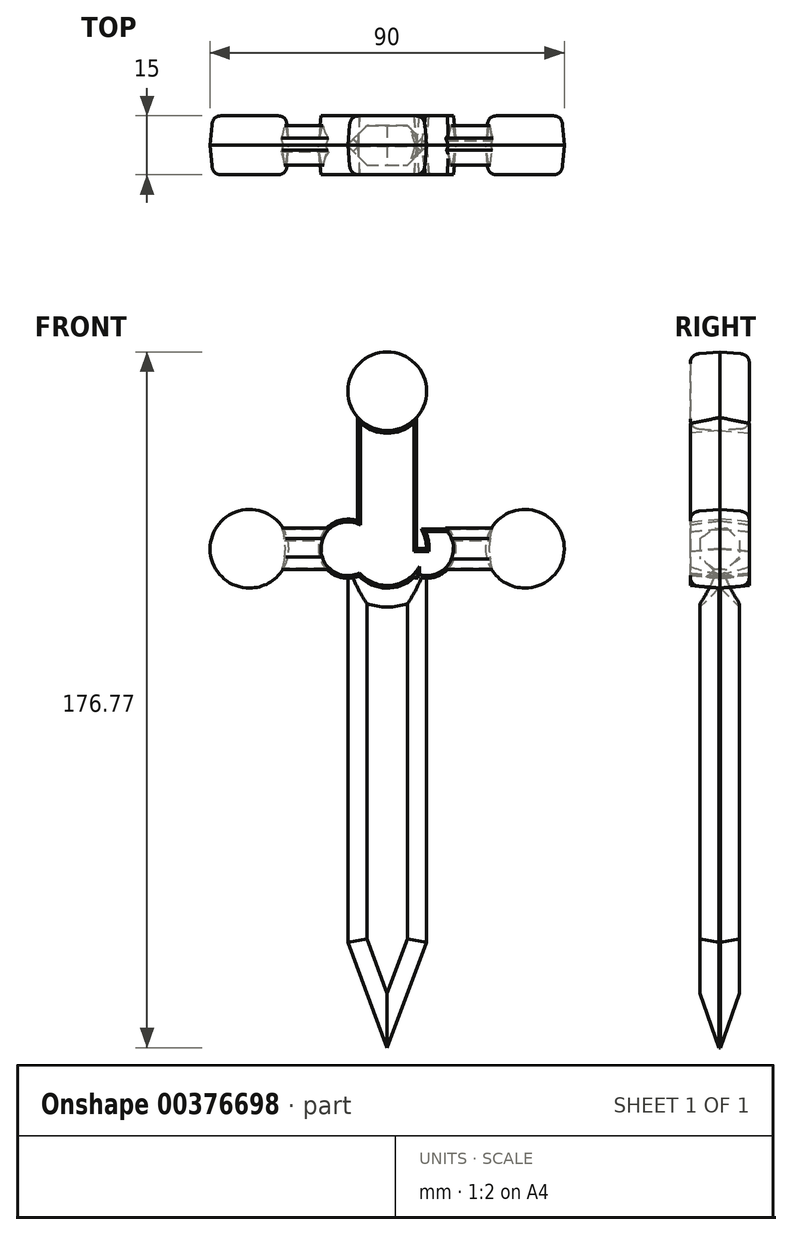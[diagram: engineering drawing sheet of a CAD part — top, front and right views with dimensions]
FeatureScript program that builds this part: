
annotation { "Feature Type Name" : "Feature", "Feature Type Description" : "" }
export const myFeature = defineFeature(function(context is Context, id is Id, definition is map)
    precondition{}
    {
        {
            var Q0;
            Q0=qCreatedBy(makeId("Front.planeOp"),FACE);
            var sketch = newSketch(context, id + "F0", { "sketchPlane" : qUnion([Q0])});
            skLineSegment(sketch, "E0.bottom", {"start": v(10, 50) * mm, "end": v(-10, 50) * mm});
            skLineSegment(sketch, "E0.top", {"start": v(10, -50) * mm, "end": v(-10, -50) * mm});
            skLineSegment(sketch, "E0.left", {"start": v(10, 50) * mm, "end": v(10, -50) * mm});
            skLineSegment(sketch, "E0.right", {"start": v(-10, 50) * mm, "end": v(-10, -50) * mm});
            skPoint(sketch, "E0.middle", {"position": v(0, 0) * mm});
            skCircle(sketch, "E1", {"center": v(0, 50) * mm, "radius": 10 * mm});
            skLineSegment(sketch, "E2.bottom", {"start": v(35, 55) * mm, "end": v(-35, 55) * mm});
            skLineSegment(sketch, "E2.top", {"start": v(35, 45) * mm, "end": v(-35, 45) * mm});
            skLineSegment(sketch, "E2.left", {"start": v(35, 55) * mm, "end": v(35, 45) * mm});
            skLineSegment(sketch, "E2.right", {"start": v(-35, 55) * mm, "end": v(-35, 45) * mm});
            skCircle(sketch, "E3", {"center": v(-35, 50) * mm, "radius": 10 * mm});
            skCircle(sketch, "E4", {"center": v(-10, 50) * mm, "radius": 7.5 * mm});
            skCircle(sketch, "E5", {"center": v(35, 50) * mm, "radius": 10 * mm});
            skCircle(sketch, "E6", {"center": v(10, 50) * mm, "radius": 7.5 * mm});
            skLineSegment(sketch, "E7.bottom", {"start": v(7.5, 90) * mm, "end": v(-7.5, 90) * mm});
            skLineSegment(sketch, "E7.top", {"start": v(7.5, 30) * mm, "end": v(-7.5, 30) * mm});
            skLineSegment(sketch, "E7.left", {"start": v(7.5, 90) * mm, "end": v(7.5, 30) * mm});
            skLineSegment(sketch, "E7.right", {"start": v(-7.5, 90) * mm, "end": v(-7.5, 30) * mm});
            skPoint(sketch, "E7.middle", {"position": v(0, 60) * mm});
            skCircle(sketch, "E8", {"center": v(0, 90) * mm, "radius": 10 * mm});
            skLineSegment(sketch, "E9", {"start": v(-10, -50) * mm, "end": v(0, -76.77) * mm});
            skLineSegment(sketch, "E10", {"start": v(0, -76.77) * mm, "end": v(10, -50) * mm});
            skSolve(sketch);
        }
        {
            var Q0;
            {var subQ0=sQuery(id+"F0.wireOp",EDGE,"E1");var subQ5=sQuery(id+"F0.wireOp",EDGE,"E2.bottom");var subQ6=makeQuery(id+"F0.imprint","INTERSECT",VERTEX,{"disambiguationData":[OD(1.0)],"derivedFrom":[subQ0,subQ5]});Q0=makeQuery(id+"F0.imprint","IMPRINT",FACE,{"disambiguationData":[TD([[makeQuery(id+"F0.imprint","IMPRINT",EDGE,{"disambiguationData":[TD([[subQ6,1.0]])],"derivedFrom":subQ5}),1.0]])]});}
            var Q1;
            {var subQ0=sQuery(id+"F0.wireOp",EDGE,"E1");var subQ5=sQuery(id+"F0.wireOp",EDGE,"E2.top");var subQ6=makeQuery(id+"F0.imprint","INTERSECT",VERTEX,{"disambiguationData":[OD(0.0)],"derivedFrom":[subQ0,subQ5]});Q1=makeQuery(id+"F0.imprint","IMPRINT",FACE,{"disambiguationData":[TD([[makeQuery(id+"F0.imprint","IMPRINT",EDGE,{"disambiguationData":[TD([[subQ6,1.0]])],"derivedFrom":subQ5}),-1.0]])]});}
            var Q2;
            {var subQ1=sQuery(id+"F0.wireOp",EDGE,"E0.right");var subQ3=sQuery(id+"F0.wireOp",EDGE,"E2.top");var subQ4=makeQuery(id+"F0.imprint","INTERSECT",VERTEX,{"derivedFrom":[subQ1,subQ3]});Q2=makeQuery(id+"F0.imprint","IMPRINT",FACE,{"disambiguationData":[TD([[makeQuery(id+"F0.imprint","IMPRINT",EDGE,{"disambiguationData":[TD([[subQ4,1.0]])],"derivedFrom":subQ3}),-1.0]])]});}
            var Q3;
            {var subQ0=sQuery(id+"F0.wireOp",EDGE,"E7.right");var subQ1=sQuery(id+"F0.wireOp",EDGE,"E1");var subQ2=makeQuery(id+"F0.imprint","INTERSECT",VERTEX,{"disambiguationData":[OD(1.0)],"derivedFrom":[subQ1,subQ0]});Q3=makeQuery(id+"F0.imprint","IMPRINT",FACE,{"disambiguationData":[TD([[makeQuery(id+"F0.imprint","IMPRINT",EDGE,{"disambiguationData":[TD([[subQ2,-1.0]])],"derivedFrom":subQ1}),1.0]])]});}
            var Q4;
            {var subQ1=sQuery(id+"F0.wireOp",EDGE,"E0.right");var subQ5=sQuery(id+"F0.wireOp",EDGE,"E4");var subQ6=makeQuery(id+"F0.imprint","INTERSECT",VERTEX,{"derivedFrom":[subQ1,subQ5]});Q4=makeQuery(id+"F0.imprint","IMPRINT",FACE,{"disambiguationData":[TD([[makeQuery(id+"F0.imprint","IMPRINT",EDGE,{"disambiguationData":[TD([[subQ6,1.0]])],"derivedFrom":subQ1}),1.0]])]});}
            var Q5;
            {var subQ0=sQuery(id+"F0.wireOp",EDGE,"E4");var subQ1=sQuery(id+"F0.wireOp",EDGE,"E0.right");var subQ2=makeQuery(id+"F0.imprint","INTERSECT",VERTEX,{"derivedFrom":[subQ1,subQ0]});Q5=makeQuery(id+"F0.imprint","IMPRINT",FACE,{"disambiguationData":[TD([[makeQuery(id+"F0.imprint","IMPRINT",EDGE,{"disambiguationData":[TD([[subQ2,1.0]])],"derivedFrom":subQ1}),-1.0]])]});}
            var Q6;
            {var subQ0=sQuery(id+"F0.wireOp",EDGE,"E2.top");var subQ1=sQuery(id+"F0.wireOp",EDGE,"E1");var subQ2=makeQuery(id+"F0.imprint","INTERSECT",VERTEX,{"disambiguationData":[OD(0.0)],"derivedFrom":[subQ1,subQ0]});Q6=makeQuery(id+"F0.imprint","IMPRINT",FACE,{"disambiguationData":[TD([[makeQuery(id+"F0.imprint","IMPRINT",EDGE,{"disambiguationData":[TD([[subQ2,-1.0]])],"derivedFrom":subQ1}),1.0]])]});}
            var Q7;
            {var subQ0=sQuery(id+"F0.wireOp",EDGE,"E4");var subQ1=sQuery(id+"F0.wireOp",EDGE,"E0.bottom");var subQ2=makeQuery(id+"F0.imprint","INTERSECT",VERTEX,{"derivedFrom":[subQ1,subQ0]});Q7=makeQuery(id+"F0.imprint","IMPRINT",FACE,{"disambiguationData":[TD([[makeQuery(id+"F0.imprint","IMPRINT",EDGE,{"disambiguationData":[TD([[subQ2,-1.0]])],"derivedFrom":subQ1}),1.0]])]});}
            var Q8;
            {var subQ0=sQuery(id+"F0.wireOp",EDGE,"E4");var subQ5=sQuery(id+"F0.wireOp",EDGE,"E2.bottom");var subQ6=makeQuery(id+"F0.imprint","INTERSECT",VERTEX,{"disambiguationData":[OD(0.0)],"derivedFrom":[subQ5,subQ0]});Q8=makeQuery(id+"F0.imprint","IMPRINT",FACE,{"disambiguationData":[TD([[makeQuery(id+"F0.imprint","IMPRINT",EDGE,{"disambiguationData":[TD([[subQ6,1.0]])],"derivedFrom":subQ5}),1.0]])]});}
            var Q9;
            {var subQ0=sQuery(id+"F0.wireOp",EDGE,"E6");var subQ1=sQuery(id+"F0.wireOp",EDGE,"E0.left");var subQ2=makeQuery(id+"F0.imprint","INTERSECT",VERTEX,{"derivedFrom":[subQ1,subQ0]});Q9=makeQuery(id+"F0.imprint","IMPRINT",FACE,{"disambiguationData":[TD([[makeQuery(id+"F0.imprint","IMPRINT",EDGE,{"disambiguationData":[TD([[subQ2,1.0]])],"derivedFrom":subQ1}),1.0]])]});}
            var Q10;
            {var subQ0=sQuery(id+"F0.wireOp",EDGE,"E6");var subQ1=sQuery(id+"F0.wireOp",EDGE,"E1");var subQ2=makeQuery(id+"F0.imprint","INTERSECT",VERTEX,{"disambiguationData":[OD(0.0)],"derivedFrom":[subQ1,subQ0]});Q10=makeQuery(id+"F0.imprint","IMPRINT",FACE,{"disambiguationData":[TD([[makeQuery(id+"F0.imprint","IMPRINT",EDGE,{"disambiguationData":[TD([[subQ2,-1.0]])],"derivedFrom":subQ1}),1.0]])]});}
            var Q11;
            {var subQ0=sQuery(id+"F0.wireOp",EDGE,"E2.left");Q11=makeQuery(id+"F0.imprint","IMPRINT",FACE,{"disambiguationData":[TD([[makeQuery(id+"F0.imprint","IMPRINT",EDGE,{"derivedFrom":subQ0}),-1.0]])]});}
            var Q12;
            {var subQ0=sQuery(id+"F0.wireOp",EDGE,"E2.right");Q12=makeQuery(id+"F0.imprint","IMPRINT",FACE,{"disambiguationData":[TD([[makeQuery(id+"F0.imprint","IMPRINT",EDGE,{"derivedFrom":subQ0}),1.0]])]});}
            var Q13;
            {var subQ0=sQuery(id+"F0.wireOp",EDGE,"E2.right");Q13=makeQuery(id+"F0.imprint","IMPRINT",FACE,{"disambiguationData":[TD([[makeQuery(id+"F0.imprint","IMPRINT",EDGE,{"derivedFrom":subQ0}),-1.0]])]});}
            var Q14;
            {var subQ0=sQuery(id+"F0.wireOp",EDGE,"E2.left");Q14=makeQuery(id+"F0.imprint","IMPRINT",FACE,{"disambiguationData":[TD([[makeQuery(id+"F0.imprint","IMPRINT",EDGE,{"derivedFrom":subQ0}),1.0]])]});}
            var Q15;
            {var subQ0=sQuery(id+"F0.wireOp",EDGE,"E2.bottom");var subQ1=sQuery(id+"F0.wireOp",EDGE,"E1");var subQ2=makeQuery(id+"F0.imprint","INTERSECT",VERTEX,{"disambiguationData":[OD(0.0)],"derivedFrom":[subQ1,subQ0]});Q15=makeQuery(id+"F0.imprint","IMPRINT",FACE,{"disambiguationData":[TD([[makeQuery(id+"F0.imprint","IMPRINT",EDGE,{"disambiguationData":[TD([[subQ2,-1.0]])],"derivedFrom":subQ1}),-1.0]])]});}
            var Q16;
            {var subQ0=sQuery(id+"F0.wireOp",EDGE,"E6");var subQ1=sQuery(id+"F0.wireOp",EDGE,"E0.bottom");var subQ2=makeQuery(id+"F0.imprint","INTERSECT",VERTEX,{"derivedFrom":[subQ1,subQ0]});Q16=makeQuery(id+"F0.imprint","IMPRINT",FACE,{"disambiguationData":[TD([[makeQuery(id+"F0.imprint","IMPRINT",EDGE,{"disambiguationData":[TD([[subQ2,-1.0]])],"derivedFrom":subQ1}),-1.0]])]});}
            var Q17;
            {var subQ0=sQuery(id+"F0.wireOp",EDGE,"E6");var subQ1=sQuery(id+"F0.wireOp",EDGE,"E0.left");var subQ2=makeQuery(id+"F0.imprint","INTERSECT",VERTEX,{"derivedFrom":[subQ1,subQ0]});Q17=makeQuery(id+"F0.imprint","IMPRINT",FACE,{"disambiguationData":[TD([[makeQuery(id+"F0.imprint","IMPRINT",EDGE,{"disambiguationData":[TD([[subQ2,1.0]])],"derivedFrom":subQ1}),-1.0]])]});}
            var Q18;
            {var subQ0=sQuery(id+"F0.wireOp",EDGE,"E4");var subQ1=sQuery(id+"F0.wireOp",EDGE,"E1");var subQ2=makeQuery(id+"F0.imprint","INTERSECT",VERTEX,{"disambiguationData":[OD(1.0)],"derivedFrom":[subQ1,subQ0]});Q18=makeQuery(id+"F0.imprint","IMPRINT",FACE,{"disambiguationData":[TD([[makeQuery(id+"F0.imprint","IMPRINT",EDGE,{"disambiguationData":[TD([[subQ2,-1.0]])],"derivedFrom":subQ1}),1.0]])]});}
            var Q19;
            {var subQ0=sQuery(id+"F0.wireOp",EDGE,"E1");var subQ5=sQuery(id+"F0.wireOp",EDGE,"E2.bottom");var subQ6=makeQuery(id+"F0.imprint","INTERSECT",VERTEX,{"disambiguationData":[OD(0.0)],"derivedFrom":[subQ0,subQ5]});Q19=makeQuery(id+"F0.imprint","IMPRINT",FACE,{"disambiguationData":[TD([[makeQuery(id+"F0.imprint","IMPRINT",EDGE,{"disambiguationData":[TD([[subQ6,-1.0]])],"derivedFrom":subQ5}),1.0]])]});}
            var Q20;
            {var subQ0=sQuery(id+"F0.wireOp",EDGE,"E6");var subQ1=sQuery(id+"F0.wireOp",EDGE,"E0.bottom");var subQ2=makeQuery(id+"F0.imprint","INTERSECT",VERTEX,{"derivedFrom":[subQ1,subQ0]});Q20=makeQuery(id+"F0.imprint","IMPRINT",FACE,{"disambiguationData":[TD([[makeQuery(id+"F0.imprint","IMPRINT",EDGE,{"disambiguationData":[TD([[subQ2,-1.0]])],"derivedFrom":subQ1}),1.0]])]});}
            var Q21;
            {var subQ0=sQuery(id+"F0.wireOp",EDGE,"E1");var subQ5=sQuery(id+"F0.wireOp",EDGE,"E2.top");var subQ6=makeQuery(id+"F0.imprint","INTERSECT",VERTEX,{"disambiguationData":[OD(1.0)],"derivedFrom":[subQ0,subQ5]});Q21=makeQuery(id+"F0.imprint","IMPRINT",FACE,{"disambiguationData":[TD([[makeQuery(id+"F0.imprint","IMPRINT",EDGE,{"disambiguationData":[TD([[subQ6,-1.0]])],"derivedFrom":subQ5}),-1.0]])]});}
            var Q22;
            {var subQ0=sQuery(id+"F0.wireOp",EDGE,"E7.right");var subQ1=sQuery(id+"F0.wireOp",EDGE,"E1");var subQ2=makeQuery(id+"F0.imprint","INTERSECT",VERTEX,{"disambiguationData":[OD(0.0)],"derivedFrom":[subQ1,subQ0]});Q22=makeQuery(id+"F0.imprint","IMPRINT",FACE,{"disambiguationData":[TD([[makeQuery(id+"F0.imprint","IMPRINT",EDGE,{"disambiguationData":[TD([[subQ2,-1.0]])],"derivedFrom":subQ1}),-1.0]])]});}
            var Q23;
            {var subQ0=sQuery(id+"F0.wireOp",EDGE,"E7.left");var subQ1=sQuery(id+"F0.wireOp",EDGE,"E1");var subQ2=makeQuery(id+"F0.imprint","INTERSECT",VERTEX,{"disambiguationData":[OD(0.0)],"derivedFrom":[subQ1,subQ0]});Q23=makeQuery(id+"F0.imprint","IMPRINT",FACE,{"disambiguationData":[TD([[makeQuery(id+"F0.imprint","IMPRINT",EDGE,{"disambiguationData":[TD([[subQ2,-1.0]])],"derivedFrom":subQ1}),1.0]])]});}
            var Q24;
            {var subQ0=sQuery(id+"F0.wireOp",EDGE,"E7.left");var subQ1=sQuery(id+"F0.wireOp",EDGE,"E0.bottom");var subQ2=makeQuery(id+"F0.imprint","INTERSECT",VERTEX,{"derivedFrom":[subQ1,subQ0]});Q24=makeQuery(id+"F0.imprint","IMPRINT",FACE,{"disambiguationData":[TD([[makeQuery(id+"F0.imprint","IMPRINT",EDGE,{"disambiguationData":[TD([[subQ2,-1.0]])],"derivedFrom":subQ1}),1.0]])]});}
            var Q25;
            {var subQ0=sQuery(id+"F0.wireOp",EDGE,"E6");var subQ5=sQuery(id+"F0.wireOp",EDGE,"E2.bottom");var subQ6=makeQuery(id+"F0.imprint","INTERSECT",VERTEX,{"disambiguationData":[OD(0.0)],"derivedFrom":[subQ5,subQ0]});Q25=makeQuery(id+"F0.imprint","IMPRINT",FACE,{"disambiguationData":[TD([[makeQuery(id+"F0.imprint","IMPRINT",EDGE,{"disambiguationData":[TD([[subQ6,-1.0]])],"derivedFrom":subQ5}),1.0]])]});}
            var Q26;
            {var subQ0=sQuery(id+"F0.wireOp",EDGE,"E6");var subQ1=sQuery(id+"F0.wireOp",EDGE,"E1");var subQ2=makeQuery(id+"F0.imprint","INTERSECT",VERTEX,{"disambiguationData":[OD(1.0)],"derivedFrom":[subQ1,subQ0]});Q26=makeQuery(id+"F0.imprint","IMPRINT",FACE,{"disambiguationData":[TD([[makeQuery(id+"F0.imprint","IMPRINT",EDGE,{"disambiguationData":[TD([[subQ2,-1.0]])],"derivedFrom":subQ1}),1.0]])]});}
            var Q27;
            {var subQ0=sQuery(id+"F0.wireOp",EDGE,"E7.left");var subQ1=sQuery(id+"F0.wireOp",EDGE,"E0.bottom");var subQ2=makeQuery(id+"F0.imprint","INTERSECT",VERTEX,{"derivedFrom":[subQ1,subQ0]});Q27=makeQuery(id+"F0.imprint","IMPRINT",FACE,{"disambiguationData":[TD([[makeQuery(id+"F0.imprint","IMPRINT",EDGE,{"disambiguationData":[TD([[subQ2,-1.0]])],"derivedFrom":subQ1}),-1.0]])]});}
            var Q28;
            {var subQ0=sQuery(id+"F0.wireOp",EDGE,"E2.bottom");var subQ1=sQuery(id+"F0.wireOp",EDGE,"E1");var subQ2=makeQuery(id+"F0.imprint","INTERSECT",VERTEX,{"disambiguationData":[OD(0.0)],"derivedFrom":[subQ1,subQ0]});Q28=makeQuery(id+"F0.imprint","IMPRINT",FACE,{"disambiguationData":[TD([[makeQuery(id+"F0.imprint","IMPRINT",EDGE,{"disambiguationData":[TD([[subQ2,-1.0]])],"derivedFrom":subQ1}),1.0]])]});}
            var Q29;
            {var subQ1=sQuery(id+"F0.wireOp",EDGE,"E0.left");var subQ3=sQuery(id+"F0.wireOp",EDGE,"E2.top");var subQ4=makeQuery(id+"F0.imprint","INTERSECT",VERTEX,{"derivedFrom":[subQ1,subQ3]});Q29=makeQuery(id+"F0.imprint","IMPRINT",FACE,{"disambiguationData":[TD([[makeQuery(id+"F0.imprint","IMPRINT",EDGE,{"disambiguationData":[TD([[subQ4,-1.0]])],"derivedFrom":subQ3}),-1.0]])]});}
            var Q30;
            {var subQ0=sQuery(id+"F0.wireOp",EDGE,"E7.left");var subQ1=sQuery(id+"F0.wireOp",EDGE,"E1");var subQ2=makeQuery(id+"F0.imprint","INTERSECT",VERTEX,{"disambiguationData":[OD(1.0)],"derivedFrom":[subQ1,subQ0]});Q30=makeQuery(id+"F0.imprint","IMPRINT",FACE,{"disambiguationData":[TD([[makeQuery(id+"F0.imprint","IMPRINT",EDGE,{"disambiguationData":[TD([[subQ2,-1.0]])],"derivedFrom":subQ1}),1.0]])]});}
            var Q31;
            {var subQ0=sQuery(id+"F0.wireOp",EDGE,"E7.left");var subQ1=sQuery(id+"F0.wireOp",EDGE,"E1");var subQ2=makeQuery(id+"F0.imprint","INTERSECT",VERTEX,{"disambiguationData":[OD(0.0)],"derivedFrom":[subQ1,subQ0]});Q31=makeQuery(id+"F0.imprint","IMPRINT",FACE,{"disambiguationData":[TD([[makeQuery(id+"F0.imprint","IMPRINT",EDGE,{"disambiguationData":[TD([[subQ2,-1.0]])],"derivedFrom":subQ1}),-1.0]])]});}
            var Q32;
            {var subQ0=sQuery(id+"F0.wireOp",EDGE,"E4");var subQ1=sQuery(id+"F0.wireOp",EDGE,"E0.bottom");var subQ2=makeQuery(id+"F0.imprint","INTERSECT",VERTEX,{"derivedFrom":[subQ1,subQ0]});Q32=makeQuery(id+"F0.imprint","IMPRINT",FACE,{"disambiguationData":[TD([[makeQuery(id+"F0.imprint","IMPRINT",EDGE,{"disambiguationData":[TD([[subQ2,-1.0]])],"derivedFrom":subQ1}),-1.0]])]});}
            var Q33;
            {var subQ0=sQuery(id+"F0.wireOp",EDGE,"E7.right");var subQ1=sQuery(id+"F0.wireOp",EDGE,"E1");var subQ2=makeQuery(id+"F0.imprint","INTERSECT",VERTEX,{"disambiguationData":[OD(0.0)],"derivedFrom":[subQ1,subQ0]});Q33=makeQuery(id+"F0.imprint","IMPRINT",FACE,{"disambiguationData":[TD([[makeQuery(id+"F0.imprint","IMPRINT",EDGE,{"disambiguationData":[TD([[subQ2,-1.0]])],"derivedFrom":subQ1}),1.0]])]});}
            var Q34;
            {var subQ0=sQuery(id+"F0.wireOp",EDGE,"E4");var subQ1=sQuery(id+"F0.wireOp",EDGE,"E1");var subQ2=makeQuery(id+"F0.imprint","INTERSECT",VERTEX,{"disambiguationData":[OD(0.0)],"derivedFrom":[subQ1,subQ0]});Q34=makeQuery(id+"F0.imprint","IMPRINT",FACE,{"disambiguationData":[TD([[makeQuery(id+"F0.imprint","IMPRINT",EDGE,{"disambiguationData":[TD([[subQ2,-1.0]])],"derivedFrom":subQ1}),1.0]])]});}
            var Q35;
            {var subQ0=sQuery(id+"F0.wireOp",EDGE,"E6");var subQ1=sQuery(id+"F0.wireOp",EDGE,"E1");var subQ2=makeQuery(id+"F0.imprint","INTERSECT",VERTEX,{"disambiguationData":[OD(1.0)],"derivedFrom":[subQ1,subQ0]});Q35=makeQuery(id+"F0.imprint","IMPRINT",FACE,{"disambiguationData":[TD([[makeQuery(id+"F0.imprint","IMPRINT",EDGE,{"disambiguationData":[TD([[subQ2,-1.0]])],"derivedFrom":subQ1}),-1.0]])]});}
            var Q36;
            {var subQ0=sQuery(id+"F0.wireOp",EDGE,"E4");var subQ1=sQuery(id+"F0.wireOp",EDGE,"E1");var subQ2=makeQuery(id+"F0.imprint","INTERSECT",VERTEX,{"disambiguationData":[OD(0.0)],"derivedFrom":[subQ1,subQ0]});Q36=makeQuery(id+"F0.imprint","IMPRINT",FACE,{"disambiguationData":[TD([[makeQuery(id+"F0.imprint","IMPRINT",EDGE,{"disambiguationData":[TD([[subQ2,-1.0]])],"derivedFrom":subQ1}),-1.0]])]});}
            var Q37;
            {var subQ0=sQuery(id+"F0.wireOp",EDGE,"E7.right");var subQ1=sQuery(id+"F0.wireOp",EDGE,"E1");var subQ2=makeQuery(id+"F0.imprint","INTERSECT",VERTEX,{"disambiguationData":[OD(1.0)],"derivedFrom":[subQ1,subQ0]});Q37=makeQuery(id+"F0.imprint","IMPRINT",FACE,{"disambiguationData":[TD([[makeQuery(id+"F0.imprint","IMPRINT",EDGE,{"disambiguationData":[TD([[subQ2,-1.0]])],"derivedFrom":subQ1}),-1.0]])]});}
            extrude(context, id + "F1", {"entities" : qUnion([Q0, Q1, Q2, Q3, Q4, Q5, Q6, Q7, Q8, Q9, Q10, Q11, Q12, Q13, Q14, Q15, Q16, Q17, Q18, Q19, Q20, Q21, Q22, Q23, Q24, Q25, Q26, Q27, Q28, Q29, Q30, Q31, Q32, Q33, Q34, Q35, Q36, Q37]), "endBound" : BoundingType.SYMMETRIC, "depth" : 15 * mm, "hasDraft" : true, "draftAngle" : 5 * degree, "draftPullDirection" : true});
        }
        {
            var Q0;
            {var subQ0=sQuery(id+"F0.wireOp",EDGE,"E4");var subQ1=sQuery(id+"F0.wireOp",EDGE,"E2.bottom");var subQ2=makeQuery(id+"F0.imprint","INTERSECT",VERTEX,{"disambiguationData":[OD(0.0)],"derivedFrom":[subQ1,subQ0]});Q0=makeQuery(id+"F0.imprint","IMPRINT",FACE,{"disambiguationData":[TD([[makeQuery(id+"F0.imprint","IMPRINT",EDGE,{"disambiguationData":[TD([[subQ2,-1.0]])],"derivedFrom":subQ1}),1.0]])]});}
            var Q1;
            {var subQ0=sQuery(id+"F0.wireOp",EDGE,"E5");var subQ1=sQuery(id+"F0.wireOp",EDGE,"E2.bottom");var subQ2=makeQuery(id+"F0.imprint","INTERSECT",VERTEX,{"derivedFrom":[subQ1,subQ0]});Q1=makeQuery(id+"F0.imprint","IMPRINT",FACE,{"disambiguationData":[TD([[makeQuery(id+"F0.imprint","IMPRINT",EDGE,{"disambiguationData":[TD([[subQ2,-1.0]])],"derivedFrom":subQ1}),1.0]])]});}
            var Q2;
            {var subQ1=sQuery(id+"F0.wireOp",EDGE,"E6");var subQ5=sQuery(id+"F0.wireOp",EDGE,"E1");var subQ6=makeQuery(id+"F0.imprint","INTERSECT",VERTEX,{"disambiguationData":[OD(0.0)],"derivedFrom":[subQ5,subQ1]});Q2=makeQuery(id+"F0.imprint","IMPRINT",FACE,{"disambiguationData":[TD([[makeQuery(id+"F0.imprint","IMPRINT",EDGE,{"disambiguationData":[TD([[subQ6,-1.0]])],"derivedFrom":subQ5}),-1.0]])]});}
            extrude(context, id + "F2", {"entities" : qUnion([Q0, Q1, Q2]), "endBound" : BoundingType.SYMMETRIC, "depth" : 10 * mm, "hasDraft" : true, "draftAngle" : 10 * degree});
        }
        {
            var Q0;
            {var subQ0=sQuery(id+"F0.wireOp",EDGE,"E7.bottom");Q0=makeQuery(id+"F0.imprint","IMPRINT",FACE,{"disambiguationData":[TD([[makeQuery(id+"F0.imprint","IMPRINT",EDGE,{"derivedFrom":subQ0}),-1.0]])]});}
            var Q1;
            {var subQ0=sQuery(id+"F0.wireOp",EDGE,"E7.bottom");Q1=makeQuery(id+"F0.imprint","IMPRINT",FACE,{"disambiguationData":[TD([[makeQuery(id+"F0.imprint","IMPRINT",EDGE,{"derivedFrom":subQ0}),1.0]])]});}
            extrude(context, id + "F3", {"entities" : qUnion([Q0, Q1]), "endBound" : BoundingType.SYMMETRIC, "depth" : 15 * mm, "hasDraft" : true, "draftAngle" : 5 * degree, "draftPullDirection" : true});
        }
        {
            var Q0;
            {var subQ1=sQuery(id+"F0.wireOp",EDGE,"E0.top");Q0=makeQuery(id+"F0.imprint","IMPRINT",FACE,{"disambiguationData":[TD([[makeQuery(id+"F0.imprint","IMPRINT",EDGE,{"derivedFrom":subQ1}),-1.0]])]});}
            var Q1;
            {var subQ9=sQuery(id+"F0.wireOp",EDGE,"E7.top");Q1=makeQuery(id+"F0.imprint","IMPRINT",FACE,{"disambiguationData":[TD([[makeQuery(id+"F0.imprint","IMPRINT",EDGE,{"derivedFrom":subQ9}),-1.0]])]});}
            var Q2;
            Q2=makeQuery(id+"F0.imprint","IMPRINT",FACE,{"disambiguationData":[TD([[makeQuery(id+"F0.imprint","IMPRINT",EDGE,{"derivedFrom":sQuery(id+"F0.wireOp",EDGE,"E0.top")}),1.0]])]});
            extrude(context, id + "F4", {"entities" : qUnion([Q0, Q1, Q2]), "endBound" : BoundingType.SYMMETRIC, "depth" : 10 * mm});
        }
        {
            var Q0;
            Q0=makeQuery(id+"F1.opExtrude","CAP_EDGE",EDGE,{"disambiguationData":[OSD([sQuery(id+"F0.wireOp",EDGE,"E3")])],"isStart":false});
            var Q1;
            Q1=makeQuery(id+"F1.opExtrude","CAP_FACE",FACE,{"disambiguationData":[OSD([sQuery(id+"F0.wireOp",EDGE,"E1"),sQuery(id+"F0.wireOp",EDGE,"E4"),sQuery(id+"F0.wireOp",EDGE,"E6")])],"isStart":false});
            var Q2;
            Q2=makeQuery(id+"F1.opExtrude","CAP_FACE",FACE,{"disambiguationData":[OSD([sQuery(id+"F0.wireOp",EDGE,"E5")])],"isStart":false});
            var Q3;
            Q3=makeQuery(id+"F3.opExtrude","CAP_EDGE",EDGE,{"disambiguationData":[OSD([sQuery(id+"F0.wireOp",EDGE,"E8")])],"isStart":false});
            var Q4;
            Q4=makeQuery(id+"F1.opExtrude","CAP_FACE",FACE,{"disambiguationData":[OSD([sQuery(id+"F0.wireOp",EDGE,"E3")])],"isStart":true});
            var Q5;
            Q5=makeQuery(id+"F1.opExtrude","CAP_FACE",FACE,{"disambiguationData":[OSD([sQuery(id+"F0.wireOp",EDGE,"E1"),sQuery(id+"F0.wireOp",EDGE,"E4"),sQuery(id+"F0.wireOp",EDGE,"E6")])],"isStart":true});
            var Q6;
            Q6=makeQuery(id+"F1.opExtrude","CAP_FACE",FACE,{"disambiguationData":[OSD([sQuery(id+"F0.wireOp",EDGE,"E5")])],"isStart":true});
            var Q7;
            Q7=makeQuery(id+"F3.opExtrude","CAP_EDGE",EDGE,{"disambiguationData":[OSD([sQuery(id+"F0.wireOp",EDGE,"E8")])],"isStart":true});
            fillet(context, id + "F5", {"entities" : qUnion([Q0, Q1, Q2, Q3, Q4, Q5, Q6, Q7]), "radius" : 2.54 * mm, "tangentPropagation" : true, "rho" : 0.5, "crossSection" : FilletCrossSection.CONIC, "allowEdgeOverflow" : false});
        }
        {
            var Q0;
            Q0=makeQuery(id+"F2.opExtrude","CAP_EDGE",EDGE,{"disambiguationData":[OSD([sQuery(id+"F0.wireOp",EDGE,"E7.left")])],"isStart":false});
            var Q1;
            Q1=makeQuery(id+"F2.opExtrude","CAP_EDGE",EDGE,{"disambiguationData":[OSD([sQuery(id+"F0.wireOp",EDGE,"E7.left")])],"isStart":true});
            var Q2;
            Q2=makeQuery(id+"F2.opExtrude","CAP_EDGE",EDGE,{"disambiguationData":[OSD([sQuery(id+"F0.wireOp",EDGE,"E7.right")])],"isStart":true});
            var Q3;
            Q3=makeQuery(id+"F2.opExtrude","CAP_EDGE",EDGE,{"disambiguationData":[OSD([sQuery(id+"F0.wireOp",EDGE,"E7.right")])],"isStart":false});
            var Q4;
            {var subQ0=sQuery(id+"F0.wireOp",EDGE,"E2.bottom");Q4=makeQuery(id+"F2.opExtrude","CAP_EDGE",EDGE,{"disambiguationData":[OSD([subQ0]),TDD([makeQuery(id+"F0.imprint","IMPRINT",EDGE,{"disambiguationData":[TD([[makeQuery(id+"F0.imprint","INTERSECT",VERTEX,{"derivedFrom":[subQ0,sQuery(id+"F0.wireOp",EDGE,"E5")]}),-1.0]])],"derivedFrom":subQ0})])],"isStart":false});}
            var Q5;
            {var subQ0=sQuery(id+"F0.wireOp",EDGE,"E2.bottom");Q5=makeQuery(id+"F2.opExtrude","CAP_EDGE",EDGE,{"disambiguationData":[OSD([subQ0]),TDD([makeQuery(id+"F0.imprint","IMPRINT",EDGE,{"disambiguationData":[TD([[makeQuery(id+"F0.imprint","INTERSECT",VERTEX,{"derivedFrom":[subQ0,sQuery(id+"F0.wireOp",EDGE,"E5")]}),-1.0]])],"derivedFrom":subQ0})])],"isStart":true});}
            var Q6;
            {var subQ0=sQuery(id+"F0.wireOp",EDGE,"E2.top");Q6=makeQuery(id+"F2.opExtrude","CAP_EDGE",EDGE,{"disambiguationData":[OSD([subQ0]),TDD([makeQuery(id+"F0.imprint","IMPRINT",EDGE,{"disambiguationData":[TD([[makeQuery(id+"F0.imprint","INTERSECT",VERTEX,{"derivedFrom":[subQ0,sQuery(id+"F0.wireOp",EDGE,"E5")]}),-1.0]])],"derivedFrom":subQ0})])],"isStart":false});}
            var Q7;
            {var subQ0=sQuery(id+"F0.wireOp",EDGE,"E2.bottom");Q7=makeQuery(id+"F2.opExtrude","CAP_EDGE",EDGE,{"disambiguationData":[OSD([subQ0]),TDD([makeQuery(id+"F0.imprint","IMPRINT",EDGE,{"disambiguationData":[TD([[makeQuery(id+"F0.imprint","INTERSECT",VERTEX,{"disambiguationData":[OD(0.0)],"derivedFrom":[subQ0,sQuery(id+"F0.wireOp",EDGE,"E4")]}),-1.0]])],"derivedFrom":subQ0})])],"isStart":true});}
            var Q8;
            {var subQ0=sQuery(id+"F0.wireOp",EDGE,"E2.bottom");Q8=makeQuery(id+"F2.opExtrude","CAP_EDGE",EDGE,{"disambiguationData":[OSD([subQ0]),TDD([makeQuery(id+"F0.imprint","IMPRINT",EDGE,{"disambiguationData":[TD([[makeQuery(id+"F0.imprint","INTERSECT",VERTEX,{"disambiguationData":[OD(0.0)],"derivedFrom":[subQ0,sQuery(id+"F0.wireOp",EDGE,"E4")]}),-1.0]])],"derivedFrom":subQ0})])],"isStart":false});}
            var Q9;
            {var subQ0=sQuery(id+"F0.wireOp",EDGE,"E2.top");Q9=makeQuery(id+"F2.opExtrude","CAP_EDGE",EDGE,{"disambiguationData":[OSD([subQ0]),TDD([makeQuery(id+"F0.imprint","IMPRINT",EDGE,{"disambiguationData":[TD([[makeQuery(id+"F0.imprint","INTERSECT",VERTEX,{"disambiguationData":[OD(0.0)],"derivedFrom":[subQ0,sQuery(id+"F0.wireOp",EDGE,"E4")]}),-1.0]])],"derivedFrom":subQ0})])],"isStart":false});}
            var Q10;
            {var subQ0=sQuery(id+"F0.wireOp",EDGE,"E2.top");Q10=makeQuery(id+"F2.opExtrude","CAP_EDGE",EDGE,{"disambiguationData":[OSD([subQ0]),TDD([makeQuery(id+"F0.imprint","IMPRINT",EDGE,{"disambiguationData":[TD([[makeQuery(id+"F0.imprint","INTERSECT",VERTEX,{"derivedFrom":[subQ0,sQuery(id+"F0.wireOp",EDGE,"E5")]}),-1.0]])],"derivedFrom":subQ0})])],"isStart":true});}
            var Q11;
            {var subQ0=sQuery(id+"F0.wireOp",EDGE,"E2.top");Q11=makeQuery(id+"F2.opExtrude","CAP_EDGE",EDGE,{"disambiguationData":[OSD([subQ0]),TDD([makeQuery(id+"F0.imprint","IMPRINT",EDGE,{"disambiguationData":[TD([[makeQuery(id+"F0.imprint","INTERSECT",VERTEX,{"disambiguationData":[OD(0.0)],"derivedFrom":[subQ0,sQuery(id+"F0.wireOp",EDGE,"E4")]}),-1.0]])],"derivedFrom":subQ0})])],"isStart":true});}
            chamfer(context, id + "F6", {"entities" : qUnion([Q0, Q1, Q2, Q3, Q4, Q5, Q6, Q7, Q8, Q9, Q10, Q11]), "chamferType" : ChamferType.OFFSET_ANGLE, "width" : 3.8 * mm, "oppositeDirection" : true, "angle" : 45 * degree, "tangentPropagation" : true});
        }
        {
            var Q0;
            Q0=makeQuery(id+"F4.opExtrude","CAP_FACE",FACE,{"disambiguationData":[OSD([sQuery(id+"F0.wireOp",EDGE,"E0.left"),sQuery(id+"F0.wireOp",EDGE,"E0.right"),sQuery(id+"F0.wireOp",EDGE,"E1"),sQuery(id+"F0.wireOp",EDGE,"E4"),sQuery(id+"F0.wireOp",EDGE,"E6"),sQuery(id+"F0.wireOp",EDGE,"E9"),sQuery(id+"F0.wireOp",EDGE,"E10")])],"isStart":true});
            var Q1;
            Q1=makeQuery(id+"F4.opExtrude","CAP_FACE",FACE,{"disambiguationData":[OSD([sQuery(id+"F0.wireOp",EDGE,"E0.left"),sQuery(id+"F0.wireOp",EDGE,"E0.right"),sQuery(id+"F0.wireOp",EDGE,"E1"),sQuery(id+"F0.wireOp",EDGE,"E4"),sQuery(id+"F0.wireOp",EDGE,"E6"),sQuery(id+"F0.wireOp",EDGE,"E9"),sQuery(id+"F0.wireOp",EDGE,"E10")])],"isStart":false});
            chamfer(context, id + "F7", {"entities" : qUnion([Q0, Q1]), "chamferType" : ChamferType.OFFSET_ANGLE, "width" : 4.83 * mm, "oppositeDirection" : false, "angle" : 45 * degree, "tangentPropagation" : true});
        }
    });
